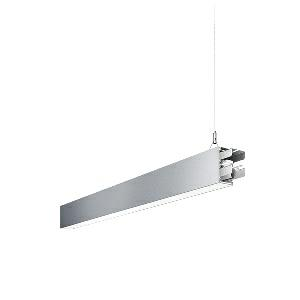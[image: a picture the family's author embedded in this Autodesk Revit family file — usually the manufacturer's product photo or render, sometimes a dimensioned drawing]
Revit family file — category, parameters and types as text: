
# Revit family: idoo_line_-_ilp_3000_vtl_d_mid_00806466_59ce
name_source: partatom
category: Lighting Fixtures
units: mm (PartAtom-declared; Revit-internal decimal feet)

## family parameters
Cut with Voids When Loaded = No
Host = Face
Light Source = No
Part Type = Normal
Room Calculation Point = No
Round Connector Dimension = Use Diameter
Shared = No

## types (1)
- IDOO.line - ILP 3000/VTL/D MID (1 x LED, 3150 lm, 2700-6500K)
    Apparent Load = 32 VA
    Approval mark = CE
    CIE Flux Codes = 66 91 98 40 100
    Color Rendering = 90-100
    Color Temperature = 2700-6500K
    Control Gear = Electronic ballast
    Default Elevation = 1800 mm
    Description = ILP 3000/VTL/D|Suspended luminaire|light source: LED|connected load: 220-240 V, 50/60 Hz|Power consumption: approx. 32 W|standby: approx. 0,25|luminous flux: 3150 lm|luminous efficacy: 98 lm/W|light distribution: Direct/indirect|direct ratio: approx. 40 %|colour temperature: Cold white, ca. 2700-6500 K|color rendering index (CRI): >= 90|chromaticity tolerance:  3 SDCM|System of protection: IP 40|technology: Continuously dimmable|luminaire body|material: Sectional aluminium|colour: Silver|lamp cover: Acrylic (PMMA), Clear|mains lead: 1,0 m With free stranded wires|Fastening: Steel cable 0.3 - 0.7 m|glare control: Prism aperture|luminance(L65): <= 2700 cd/m|unified glare rating(4H 8H): <=  16|special features: Specified values at approx. 4000 K, DALI Load 1x, Through-wired, up to 18 m on one mains connection, External control required for Dali Device type 8, Flicker-free, Constant luminous flux between 2700 and 6500 K, Constant colour temperature over the whole dimming range, Suitable as emergency lighting, Mechanical and electrical connection of the individual modules without tools|
    Frequency = 50 Hz
    Height = 110 mm
    Lamp = 1 x LED
    Lamp Light Flux = 3150 lm
    Lamp count = 1
    Length = 1122 mm
    Luminous efficacy = 98 lm/W
    Manufacturer = Waldmann
    ModVariant = No
    Model = 00806466
    Mounting Place = Ceiling
    Mounting Type = Pendant
    Number of Poles = 1
    OnlyDefault = Yes
    Power Factor = 1
    Product Name = IDOO.line - ILP 3000/VTL/D MID
    Product group = Suspended luminaire
    ProductGroupID = 9
    Protection Class = Protection class I
    Protection Degree = IP 40
    RLX_Detail_Level = 1
    RLX_Emergency_Light_Flux = 0 lm
    RLX_Emergency_Type = 0
    RLX_Emergency_Type_DB = No
    RlxData = <blob elided: 21285 chars, md5=2608a8c3>
    Socket = socket
    Standby Power = 0 W
    System Light Flux = 3150 lm
    System Power = 32 W
    Type Comments = Product without accessories
    Type Image = 113305000-00692579.jpg
    URL = http://relux.com
    VarID = ---
    Voltage = 230 V
    Voltage Range = 220-240 V
    Weight = 0.00 kg
    Width = 60 mm  [stored 0.19685 ft]

note: [stored X ft] marks values corroborated as IEEE doubles in the binary element streams (Revit-internal decimal feet)

## geometry (parser evidence)
native form markers: Blend x4, Sweep x13
no freeform markers — native parametric forms only
